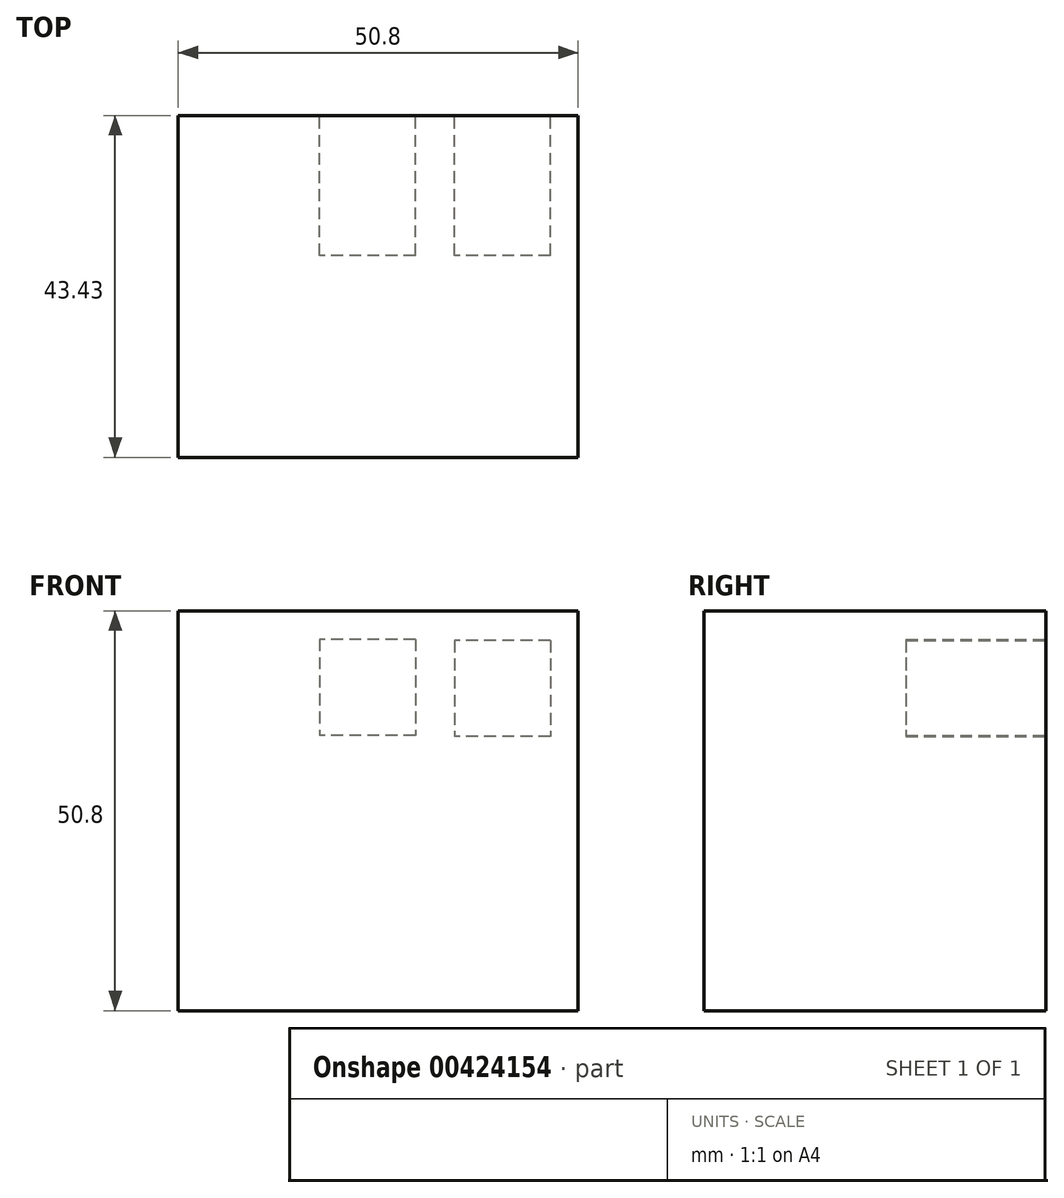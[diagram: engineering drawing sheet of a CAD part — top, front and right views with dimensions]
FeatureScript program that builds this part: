
annotation { "Feature Type Name" : "Feature", "Feature Type Description" : "" }
export const myFeature = defineFeature(function(context is Context, id is Id, definition is map)
    precondition{}
    {
        {
            var Q0;
            Q0=qCreatedBy(makeId("Front.planeOp"),FACE);
            var sketch = newSketch(context, id + "F0", { "sketchPlane" : qUnion([Q0])});
            skLineSegment(sketch, "E0.bottom", {"start": v(-24.58, 28.46) * mm, "end": v(26.22, 28.46) * mm});
            skLineSegment(sketch, "E0.top", {"start": v(-24.58, -22.34) * mm, "end": v(26.22, -22.34) * mm});
            skLineSegment(sketch, "E0.left", {"start": v(-24.58, 28.46) * mm, "end": v(-24.58, -22.34) * mm});
            skLineSegment(sketch, "E0.right", {"start": v(26.22, 28.46) * mm, "end": v(26.22, -22.34) * mm});
            skSolve(sketch);
        }
        {
            var Q0;
            Q0 = qSketchRegion(id + "F0", true);
            extrude(context, id + "F1", {"entities" : qUnion([Q0]), "depth" : 43.43 * mm});
        }
        {
            var Q0;
            Q0=makeQuery(id+"F1.opExtrude","CAP_FACE",FACE,{"disambiguationData":[OSD([sQuery(id+"F0.wireOp",EDGE,"E0.bottom"),sQuery(id+"F0.wireOp",EDGE,"E0.top"),sQuery(id+"F0.wireOp",EDGE,"E0.left"),sQuery(id+"F0.wireOp",EDGE,"E0.right")])],"isStart":true});
            var sketch = newSketch(context, id + "F2", { "sketchPlane" : qUnion([Q0])});
            skLineSegment(sketch, "E1.bottom", {"start": v(-22.7, 24.69) * mm, "end": v(-10.5, 24.69) * mm});
            skLineSegment(sketch, "E1.top", {"start": v(-22.7, 12.5) * mm, "end": v(-10.5, 12.5) * mm});
            skLineSegment(sketch, "E1.left", {"start": v(-22.7, 24.69) * mm, "end": v(-22.7, 12.5) * mm});
            skLineSegment(sketch, "E1.right", {"start": v(-10.5, 24.69) * mm, "end": v(-10.5, 12.5) * mm});
            skSolve(sketch);
        }
        {
            var Q0;
            Q0=makeQuery(id+"F2.imprint","IMPRINT",FACE,{"disambiguationData":[TD([[makeQuery(id+"F2.imprint","IMPRINT",EDGE,{"derivedFrom":sQuery(id+"F2.wireOp",EDGE,"E1.bottom")}),-1.0]])]});
            extrude(context, id + "F3", {"entities" : qUnion([Q0]), "operationType" : NewBodyOperationType.REMOVE, "oppositeDirection" : true, "depth" : 17.78 * mm});
        }
        {
            var Q0;
            Q0=makeQuery(id+"F1.opExtrude","CAP_FACE",FACE,{"disambiguationData":[OSD([sQuery(id+"F0.wireOp",EDGE,"E0.bottom"),sQuery(id+"F0.wireOp",EDGE,"E0.top"),sQuery(id+"F0.wireOp",EDGE,"E0.left"),sQuery(id+"F0.wireOp",EDGE,"E0.right")])],"isStart":true});
            var sketch = newSketch(context, id + "F4", { "sketchPlane" : qUnion([Q0])});
            skLineSegment(sketch, "E2.bottom", {"start": v(-5.55, 24.85) * mm, "end": v(6.64, 24.85) * mm});
            skLineSegment(sketch, "E2.top", {"start": v(-5.55, 12.65) * mm, "end": v(6.64, 12.65) * mm});
            skLineSegment(sketch, "E2.left", {"start": v(-5.55, 24.85) * mm, "end": v(-5.55, 12.65) * mm});
            skLineSegment(sketch, "E2.right", {"start": v(6.64, 24.85) * mm, "end": v(6.64, 12.65) * mm});
            skSolve(sketch);
        }
        {
            var Q0;
            Q0 = qSketchRegion(id + "F4", true);
            extrude(context, id + "F5", {"entities" : qUnion([Q0]), "operationType" : NewBodyOperationType.REMOVE, "oppositeDirection" : true, "depth" : 17.78 * mm});
        }
    });
